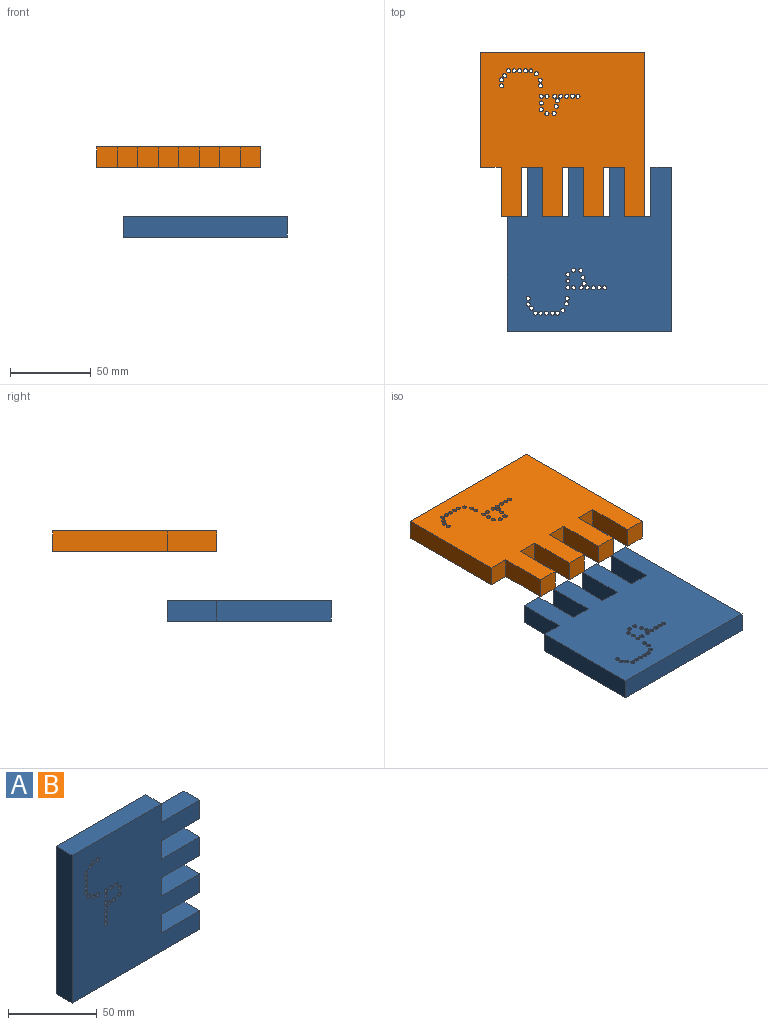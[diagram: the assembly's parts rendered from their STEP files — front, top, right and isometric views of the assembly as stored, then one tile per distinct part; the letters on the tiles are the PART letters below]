
ASSEMBLY  parts=2 mates=1
PART A: 44 faces, bbox 101.6x12.7x101.6 mm
  f0: plane 71.12x12.7mm, normal (0,0,1), area 903.2mm2, adj f1,f40,f42,f43
  f1: plane 101.6x12.7mm, normal (-1,0,0), area 1290.3mm2, adj f0,f2,f42,f43
  f2: plane 101.6x12.7mm, normal (0,0,-1), area 1290.3mm2, adj f1,f3,f42,f43
  f3: plane 12.7x12.7mm, normal (1,0,0), area 161.3mm2, adj f2,f4,f42,f43
  f4: plane 30.48x12.7mm, normal (0,0,1), area 387.1mm2, adj f3,f5,f42,f43
  f5: plane 12.7x12.7mm, normal (1,0,0), area 161.3mm2, adj f4,f6,f42,f43
  f6: plane 30.48x12.7mm, normal (0,0,-1), area 387.1mm2, adj f5,f7,f42,f43
  f7: plane 12.7x12.7mm, normal (1,0,0), area 161.3mm2, adj f6,f8,f42,f43
  f8: plane 30.48x12.7mm, normal (0,0,1), area 387.1mm2, adj f7,f9,f42,f43
  f9: plane 12.7x12.7mm, normal (1,0,0), area 161.3mm2, adj f8,f10,f42,f43
  f10: plane 30.48x12.7mm, normal (0,0,-1), area 387.1mm2, adj f9,f11,f42,f43
  f11: plane 12.7x12.7mm, normal (1,0,0), area 161.3mm2, adj f10,f12,f42,f43
  f12: plane 30.48x12.7mm, normal (0,0,1), area 387.1mm2, adj f11,f13,f42,f43
  f13: plane 12.7x12.7mm, normal (1,0,0), area 161.3mm2, adj f12,f14,f42,f43
  f14: plane 30.48x12.7mm, normal (0,0,-1), area 387.1mm2, adj f13,f15,f42,f43
  f15: plane 12.7x12.7mm, normal (1,0,0), area 161.3mm2, adj f14,f16,f42,f43
  f16: plane 30.48x12.7mm, normal (0,0,1), area 387.1mm2, adj f15,f40,f42,f43
  f17: cylinder r=1.27mm len=12.7mm, axis (0,1,0), area 101.3mm2, adj f42,f43
  f18: cylinder r=1.27mm len=12.7mm, axis (0,1,0), area 101.3mm2, adj f42,f43
  f19: cylinder r=1.27mm len=12.7mm, axis (0,1,0), area 101.3mm2, adj f42,f43
  f20: cylinder r=1.27mm len=12.7mm, axis (0,1,0), area 101.3mm2, adj f42,f43
  f21: cylinder r=1.27mm len=12.7mm, axis (0,1,0), area 101.3mm2, adj f42,f43
  f22: cylinder r=1.27mm len=12.7mm, axis (0,1,0), area 101.3mm2, adj f42,f43
  f23: cylinder r=1.27mm len=12.7mm, axis (0,1,0), area 101.3mm2, adj f42,f43
  f24: cylinder r=1.27mm len=12.7mm, axis (0,1,0), area 101.3mm2, adj f42,f43
  f25: cylinder r=1.27mm len=12.7mm, axis (0,1,0), area 101.3mm2, adj f42,f43
  f26: cylinder r=1.27mm len=12.7mm, axis (0,1,0), area 101.3mm2, adj f42,f43
  f27: cylinder r=1.27mm len=12.7mm, axis (0,1,0), area 101.3mm2, adj f42,f43
  f28: cylinder r=1.27mm len=12.7mm, axis (0,1,0), area 101.3mm2, adj f42,f43
  f29: cylinder r=1.27mm len=12.7mm, axis (0,1,0), area 101.3mm2, adj f42,f43
  f30: cylinder r=1.27mm len=12.7mm, axis (0,1,0), area 101.3mm2, adj f42,f43
  f31: cylinder r=1.27mm len=12.7mm, axis (0,1,0), area 101.3mm2, adj f42,f43
  f32: cylinder r=1.27mm len=12.7mm, axis (0,1,0), area 101.3mm2, adj f42,f43
  f33: cylinder r=1.27mm len=12.7mm, axis (0,1,0), area 101.3mm2, adj f42,f43
  f34: cylinder r=1.27mm len=12.7mm, axis (0,1,0), area 101.3mm2, adj f42,f43
  f35: cylinder r=1.27mm len=12.7mm, axis (0,1,0), area 101.3mm2, adj f42,f43
  f36: cylinder r=1.27mm len=12.7mm, axis (0,1,0), area 101.3mm2, adj f42,f43
  f37: cylinder r=1.27mm len=12.7mm, axis (0,1,0), area 101.3mm2, adj f42,f43
  f38: cylinder r=1.27mm len=12.7mm, axis (0,1,0), area 101.3mm2, adj f42,f43
  f39: cylinder r=1.27mm len=12.7mm, axis (0,1,0), area 101.3mm2, adj f42,f43
  f40: plane 12.7x12.7mm, normal (1,0,0), area 161.3mm2, adj f0,f16,f42,f43
  f41: cylinder r=1.27mm len=12.7mm, axis (0,1,0), area 101.3mm2, adj f42,f43
  f42: plane 101.6x101.6mm, normal (0,-1,0), area 8652.6mm2, adj f0,f1,f2,f3,f4,f5,f6,f7
  f43: plane 101.6x101.6mm, normal (0,1,0), area 8652.6mm2, adj f0,f1,f2,f3,f4,f5,f6,f7
PART B: same geometry as A
PLACE A rot(axis=(-0.58,-0.58,0.58),120deg) t=(-226.77,-212.38,-168.05)mm
PLACE B rot(axis=(0.58,-0.58,-0.58),120deg) t=(-243.25,-140.44,-112.27)mm
MATE parallel A.f14 <-> B.f4  axis (-1,0,0) through (-243.82,-161.08,-155.35)mm
